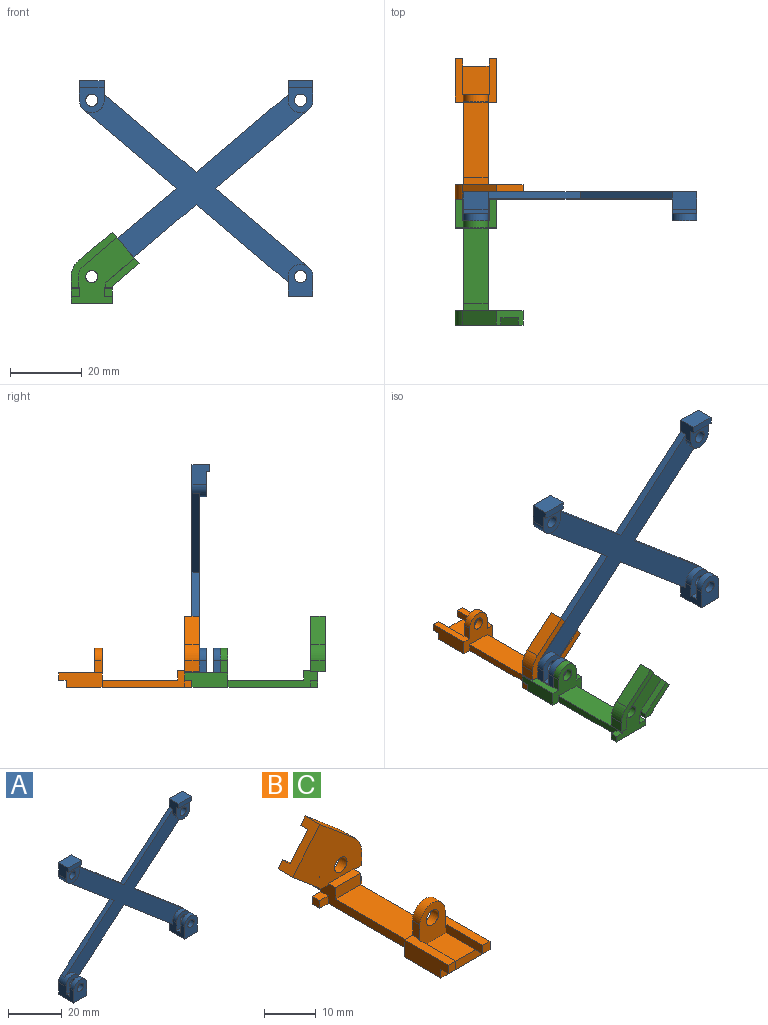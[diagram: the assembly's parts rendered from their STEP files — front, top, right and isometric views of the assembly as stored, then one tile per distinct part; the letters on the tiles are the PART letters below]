
ASSEMBLY  parts=3 mates=2
PART A: 48 faces, bbox 64.9x8x59.9 mm
  f0: plane 6.88x2mm, normal (0,0,1), area 13.8mm2, adj f1,f4,f6,f24
  f1: plane 6.88x6.88mm, normal (0,-1,0), area 33.2mm2, adj f0,f3,f4,f6,f8
  f2: plane 25.89x21.87mm, normal (-0.65,0,0.76), area 67.8mm2, adj f3,f9,f10,f11
  f3: cylinder r=3.44mm len=6.88mm, axis (0,1,0), area 27.6mm2, adj f1,f2,f4,f6,f9,f10
  f4: plane 8x5.44mm, normal (-1,0,0), area 36.6mm2, adj f0,f1,f3,f5,f10,f21,f22,f24
  f5: plane 8x6.88mm, normal (0,0,-1), area 55mm2, adj f4,f6,f10,f21
  f6: plane 8x5.44mm, normal (1,0,0), area 33.4mm2, adj f0,f1,f3,f5,f7,f9,f10,f21
  f7: plane 25.56x21.59mm, normal (0.65,0,-0.76), area 66.9mm2, adj f6,f9,f10,f32
  f8: cylinder r=1.7mm len=4mm, axis (0,1,0), area 42.7mm2, adj f1,f10
  f9: plane 62.44x52.19mm, normal (0,-1,0), area 921mm2, adj f2,f3,f6,f7,f11,f12,f15,f16
  f10: plane 64.88x59.88mm, normal (0,1,0), area 1108.7mm2, adj f2,f3,f4,f5,f6,f7,f8,f11
  f11: plane 25.89x21.87mm, normal (-0.65,0,-0.76), area 67.8mm2, adj f2,f9,f10,f12
  f12: cylinder r=3.44mm len=6.88mm, axis (0,1,0), area 27.6mm2, adj f9,f10,f11,f13,f15,f18
  f13: plane 5.44x5mm, normal (-1,0,0), area 23.8mm2, adj f10,f12,f14,f18,f19,f20
  f14: plane 6.88x5mm, normal (0,0,1), area 34.4mm2, adj f10,f13,f15,f20
  f15: plane 5.44x5mm, normal (1,0,0), area 20.6mm2, adj f9,f10,f12,f14,f16,f18,f19,f20
  f16: plane 25.56x21.59mm, normal (0.65,0,0.76), area 66.9mm2, adj f9,f10,f15,f39
  f17: cylinder r=1.7mm len=4mm, axis (0,1,0), area 42.7mm2, adj f10,f18
  f18: plane 6.88x6.88mm, normal (0,-1,0), area 33.2mm2, adj f12,f13,f15,f17,f19
  f19: plane 6.88x1mm, normal (0,0,-1), area 6.9mm2, adj f13,f15,f18,f20
  f20: plane 6.88x2mm, normal (0,-1,0), area 13.8mm2, adj f13,f14,f15,f19
  f21: plane 8.88x6.88mm, normal (0,-1,0), area 46.9mm2, adj f4,f5,f6,f22,f23
  f22: cylinder r=3.44mm len=6.88mm, axis (0,1,0), area 21.6mm2, adj f4,f6,f21,f24
  f23: cylinder r=1.7mm len=3.4mm, axis (0,1,0), area 21.4mm2, adj f21,f24
  f24: plane 6.88x6.88mm, normal (0,1,0), area 33.2mm2, adj f0,f4,f6,f22,f23
  f25: plane 6.88x2mm, normal (0,0,1), area 13.8mm2, adj f26,f29,f31,f47
  f26: plane 6.88x6.88mm, normal (0,-1,0), area 33.2mm2, adj f25,f28,f29,f31,f33
  f27: plane 25.89x21.87mm, normal (0.65,0,0.76), area 67.8mm2, adj f9,f10,f28,f34
  f28: cylinder r=3.44mm len=6.88mm, axis (0,1,0), area 27.6mm2, adj f9,f10,f26,f27,f29,f31
  f29: plane 8x5.44mm, normal (1,0,0), area 36.6mm2, adj f10,f25,f26,f28,f30,f44,f45,f47
  f30: plane 8x6.88mm, normal (0,0,-1), area 55mm2, adj f10,f29,f31,f44
  f31: plane 8x5.44mm, normal (-1,0,0), area 33.4mm2, adj f9,f10,f25,f26,f28,f30,f32,f44
  f32: plane 25.56x21.59mm, normal (-0.65,0,-0.76), area 66.9mm2, adj f7,f9,f10,f31
  f33: cylinder r=1.7mm len=4mm, axis (0,1,0), area 42.7mm2, adj f10,f26
  f34: plane 25.89x21.87mm, normal (0.65,0,-0.76), area 67.8mm2, adj f9,f10,f27,f35
  f35: cylinder r=3.44mm len=6.88mm, axis (0,1,0), area 27.6mm2, adj f9,f10,f34,f36,f38,f41
  f36: plane 5.44x5mm, normal (1,0,0), area 23.8mm2, adj f10,f35,f37,f41,f42,f43
  f37: plane 6.88x5mm, normal (0,0,1), area 34.4mm2, adj f10,f36,f38,f43
  f38: plane 5.44x5mm, normal (-1,0,0), area 20.6mm2, adj f9,f10,f35,f37,f39,f41,f42,f43
  f39: plane 25.56x21.59mm, normal (-0.65,0,0.76), area 66.9mm2, adj f9,f10,f16,f38
  f40: cylinder r=1.7mm len=4mm, axis (0,1,0), area 42.7mm2, adj f10,f41
  f41: plane 6.88x6.88mm, normal (0,-1,0), area 33.2mm2, adj f35,f36,f38,f40,f42
  f42: plane 6.88x1mm, normal (0,0,-1), area 6.9mm2, adj f36,f38,f41,f43
  f43: plane 6.88x2mm, normal (0,-1,0), area 13.8mm2, adj f36,f37,f38,f42
  f44: plane 8.88x6.88mm, normal (0,-1,0), area 46.9mm2, adj f29,f30,f31,f45,f46
  f45: cylinder r=3.44mm len=6.88mm, axis (0,1,0), area 21.6mm2, adj f29,f31,f44,f47
  f46: cylinder r=1.7mm len=3.4mm, axis (0,1,0), area 21.4mm2, adj f44,f47
  f47: plane 6.88x6.88mm, normal (0,1,0), area 33.2mm2, adj f25,f29,f31,f45,f46
PART B: 50 faces, bbox 18.9x39x19.8 mm
  f0: plane 18.87x15.38mm, normal (0,-1,0), area 164.4mm2, adj f6,f7,f17,f18,f19,f20,f21,f22
  f1: plane 2x2mm, normal (0,-1,0), area 4mm2, adj f5,f11,f12,f34
  f2: plane 12x4mm, normal (1,0,0), area 44mm2, adj f4,f9,f10,f15,f33,f35
  f3: plane 8x7.38mm, normal (0,0,1), area 59mm2, adj f12,f13,f14,f35
  f4: plane 35x11.5mm, normal (0,0,-1), area 295mm2, adj f2,f6,f7,f9,f11,f16,f23,f24
  f5: plane 12x2.25mm, normal (0,0,1), area 24.5mm2, adj f1,f9,f11,f12,f13,f32
  f6: plane 25x4.72mm, normal (1,0,0), area 56.6mm2, adj f0,f4,f8,f9,f16,f22,f26,f27
  f7: plane 25x4.72mm, normal (-1,0,0), area 56.6mm2, adj f0,f4,f8,f9,f16,f18,f24,f25
  f8: plane 21x6.88mm, normal (0,0,1), area 144.5mm2, adj f6,f7,f9,f49
  f9: plane 11.38x10.88mm, normal (0,1,0), area 64.9mm2, adj f2,f4,f5,f6,f7,f8,f11,f15
  f10: plane 2x2mm, normal (0,-1,0), area 4mm2, adj f2,f14,f15,f33
  f11: plane 12x4mm, normal (-1,0,0), area 44mm2, adj f1,f4,f5,f9,f34,f35
  f12: plane 10x2mm, normal (1,0,0), area 20mm2, adj f1,f3,f5,f13,f34
  f13: plane 8.88x7.38mm, normal (0,-1,0), area 47.9mm2, adj f3,f5,f12,f14,f15,f29,f30,f31
  f14: plane 10x2mm, normal (-1,0,0), area 20mm2, adj f3,f10,f13,f15,f33
  f15: plane 12x2.25mm, normal (0,0,1), area 24.5mm2, adj f2,f9,f10,f13,f14,f30
  f16: plane 18.25x17.58mm, normal (0,1,0), area 144.3mm2, adj f4,f6,f7,f17,f18,f19,f20,f21
  f17: cylinder r=1.7mm len=3.4mm, axis (0,1,0), area 21.4mm2, adj f0,f16
  f18: plane 4x2.31mm, normal (0,0,-1), area 8.6mm2, adj f0,f7,f16,f44,f45,f47
  f19: cylinder r=5.75mm len=2mm, axis (0,1,0), area 0.1mm2, adj f0,f16,f20,f43
  f20: plane 2x0.05mm, normal (1,0,0), area 0.1mm2, adj f0,f16,f19,f43
  f21: plane 8.78x7.42mm, normal (-0.76,0,0.65), area 31mm2, adj f0,f16,f36,f39,f42,f43,f46,f47
  f22: plane 4x2.31mm, normal (0,0,-1), area 8.6mm2, adj f0,f6,f16,f37,f41,f42
  f23: plane 2x1.8mm, normal (-1,0,0), area 3.6mm2, adj f4,f16,f24,f25
  f24: plane 2.31x1.8mm, normal (0,-1,0), area 4.2mm2, adj f4,f7,f23,f25
  f25: plane 2.31x2mm, normal (0,0,1), area 4.6mm2, adj f7,f16,f23,f24
  f26: plane 2.31x1.8mm, normal (0,-1,0), area 4.2mm2, adj f4,f6,f27,f28
  f27: plane 2.31x2mm, normal (0,0,1), area 4.6mm2, adj f6,f16,f26,f28
  f28: plane 2x1.8mm, normal (1,0,0), area 3.6mm2, adj f4,f16,f26,f27
  f29: cylinder r=3.44mm len=6.88mm, axis (0,1,0), area 21.6mm2, adj f9,f13,f30,f32
  f30: plane 3.44x2mm, normal (1,0,0), area 6.9mm2, adj f9,f13,f15,f29
  f31: cylinder r=1.7mm len=3.4mm, axis (0,1,0), area 21.4mm2, adj f9,f13
  f32: plane 3.44x2mm, normal (-1,0,0), area 6.9mm2, adj f5,f9,f13,f29
  f33: plane 2x2mm, normal (0,0,-1), area 4mm2, adj f2,f10,f14,f35
  f34: plane 2x2mm, normal (0,0,-1), area 4mm2, adj f1,f11,f12,f35
  f35: plane 11.38x2mm, normal (0,-1,0), area 22.8mm2, adj f2,f3,f4,f11,f33,f34
  f36: plane 9.41x7.95mm, normal (-0.65,0,-0.76), area 24.6mm2, adj f16,f21,f38,f42
  f37: plane 3.04x2mm, normal (-1,0,0), area 6.1mm2, adj f16,f22,f38,f42
  f38: cylinder r=3.75mm len=2.86mm, axis (0,-1,0), area 6.5mm2, adj f16,f36,f37,f42
  f39: plane 9.41x7.95mm, normal (0.65,0,0.76), area 49.3mm2, adj f0,f21,f40,f42
  f40: cylinder r=5.75mm len=4.39mm, axis (0,-1,0), area 20mm2, adj f0,f39,f41,f42
  f41: plane 4x3.04mm, normal (1,0,0), area 12.2mm2, adj f0,f22,f40,f42
  f42: plane 15.38x12.74mm, normal (0,1,0), area 39mm2, adj f21,f22,f36,f37,f38,f39,f40,f41
  f43: plane 8.08x6.83mm, normal (0.65,0,0.76), area 21.2mm2, adj f0,f16,f19,f20,f21,f44,f47
  f44: plane 2x1.3mm, normal (1,0,0), area 2.6mm2, adj f16,f18,f43,f47
  f45: plane 4x0.37mm, normal (-1,0,0), area 1.5mm2, adj f0,f18,f46,f47
  f46: plane 7.37x6.23mm, normal (-0.65,0,-0.76), area 38.6mm2, adj f0,f21,f45,f47
  f47: plane 9.37x8.13mm, normal (0,1,0), area 21.9mm2, adj f18,f21,f43,f44,f45,f46
  f48: plane 6.88x2mm, normal (0,0,1), area 13.8mm2, adj f0,f6,f7,f49
  f49: plane 6.88x2.72mm, normal (0,-1,0), area 18.7mm2, adj f6,f7,f8,f48
PART C: same geometry as B
PLACE A t=(-24.84,2.81,2.12)mm fixed
PLACE B rot(axis=(0,0,-1),180deg) t=(-24.84,35.7,-5.32)mm
PLACE C rot(axis=(0,0,-1),180deg) t=(-24.84,0.7,-5.32)mm
MATE fastened A.f8 <-> C.f31  axis (0,-1,0) through (-24.84,-5.19,2.12)mm
MATE fastened A.f8 <-> B.f17  axis (0,1,0) through (-24.84,2.81,2.12)mm
